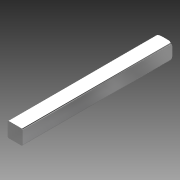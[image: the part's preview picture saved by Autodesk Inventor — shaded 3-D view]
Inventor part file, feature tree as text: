
AUTODESK INVENTOR PART (.ipt)
format: ipt  version: 2012 (Build 160160000, 160)  size: 121,344 bytes
history: native  units: in
note: dims shown in document units (in); Inventor stores cm internally (conversion verified against a paired STEP export)
features: other x1, imported_body x1, plane x1, split x1
ambient origin geometry x8: Origin, YZ Plane, XZ Plane, XY Plane, X Axis, Y Axis, Z Axis, Center Point
feature tree (4):
  parser-record x1  (decoder bookkeeping rows leaked as tree rows — omitted from the tree; the rows remain in map.json)
  imported_body  "Base1"
  plane  "Work Plane1"
  split  "Split1"
